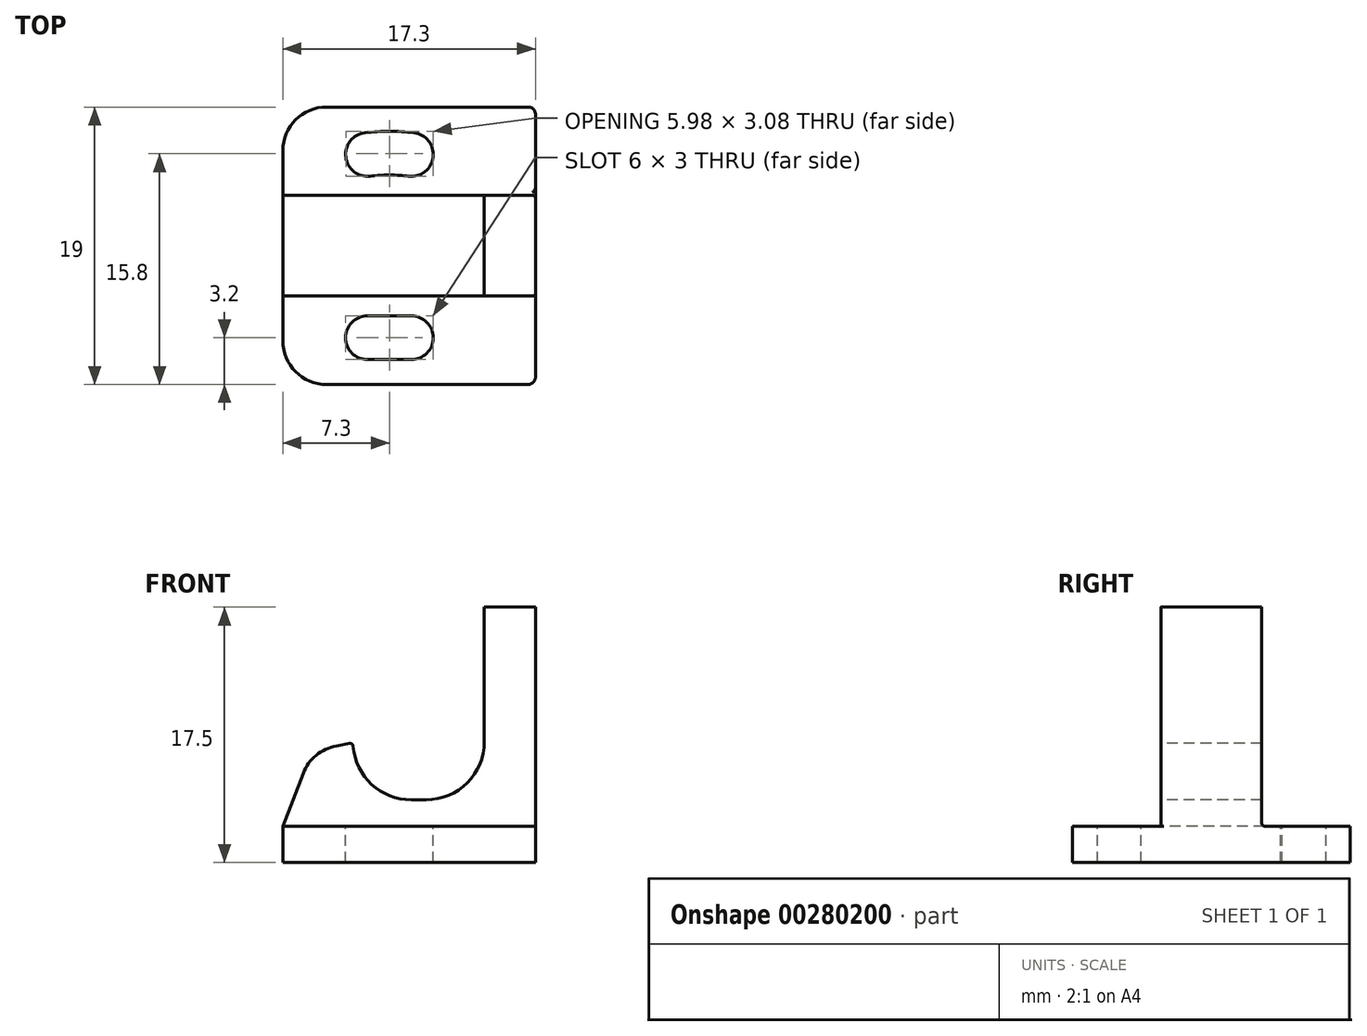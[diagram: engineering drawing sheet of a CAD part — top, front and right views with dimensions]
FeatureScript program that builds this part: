
annotation { "Feature Type Name" : "Feature", "Feature Type Description" : "" }
export const myFeature = defineFeature(function(context is Context, id is Id, definition is map)
    precondition{}
    {
        {
            var Q0;
            Q0=qCreatedBy(makeId("Top.planeOp"),FACE);
            var sketch = newSketch(context, id + "F0", { "sketchPlane" : qUnion([Q0])});
            skLineSegment(sketch, "E0.bottom", {"start": v(-8.65, 9.5) * mm, "end": v(8.65, 9.5) * mm});
            skLineSegment(sketch, "E0.top", {"start": v(-8.65, -9.5) * mm, "end": v(8.65, -9.5) * mm});
            skLineSegment(sketch, "E0.left", {"start": v(-8.65, 9.5) * mm, "end": v(-8.65, -9.5) * mm});
            skLineSegment(sketch, "E0.right", {"start": v(8.65, 9.5) * mm, "end": v(8.65, -9.5) * mm});
            skPoint(sketch, "E0.middle", {"position": v(0, 0) * mm});
            skSolve(sketch);
        }
        {
            var Q0;
            Q0=makeQuery(id+"F0.imprint","IMPRINT",FACE,{"disambiguationData":[TD([[makeQuery(id+"F0.imprint","IMPRINT",EDGE,{"derivedFrom":sQuery(id+"F0.wireOp",EDGE,"E0.bottom")}),-1.0]])]});
            extrude(context, id + "F1", {"entities" : qUnion([Q0]), "depth" : 2.5 * mm});
        }
        {
            var Q0;
            Q0=makeQuery(id+"F1.opExtrude","CAP_FACE",FACE,{"disambiguationData":[OSD([sQuery(id+"F0.wireOp",EDGE,"E0.bottom"),sQuery(id+"F0.wireOp",EDGE,"E0.top"),sQuery(id+"F0.wireOp",EDGE,"E0.left"),sQuery(id+"F0.wireOp",EDGE,"E0.right")])],"isStart":false});
            var sketch = newSketch(context, id + "F2", { "sketchPlane" : qUnion([Q0])});
            skLineSegment(sketch, "E1.bottom", {"start": v(-8.65, 3.45) * mm, "end": v(8.65, 3.45) * mm});
            skLineSegment(sketch, "E1.top", {"start": v(-8.65, -3.45) * mm, "end": v(8.65, -3.45) * mm});
            skLineSegment(sketch, "E1.left", {"start": v(-8.65, 3.45) * mm, "end": v(-8.65, -3.45) * mm});
            skLineSegment(sketch, "E1.right", {"start": v(8.65, 3.45) * mm, "end": v(8.65, -3.45) * mm});
            skLineSegment(sketch, "E2", {"start": v(-8.65, 0) * mm, "end": v(8.65, 0) * mm, "construction": true});
            skLineSegment(sketch, "E3.bottom", {"start": v(8.65, 3.45) * mm, "end": v(5.15, 3.45) * mm});
            skLineSegment(sketch, "E3.top", {"start": v(8.65, 9.5) * mm, "end": v(5.15, 9.5) * mm});
            skLineSegment(sketch, "E3.left", {"start": v(8.65, 3.45) * mm, "end": v(8.65, 9.5) * mm});
            skLineSegment(sketch, "E3.right", {"start": v(5.15, 3.45) * mm, "end": v(5.15, 9.5) * mm});
            skLineSegment(sketch, "E4.bottom", {"start": v(8.65, -3.45) * mm, "end": v(5.15, -3.45) * mm});
            skLineSegment(sketch, "E4.top", {"start": v(8.65, -9.5) * mm, "end": v(5.15, -9.5) * mm});
            skLineSegment(sketch, "E4.left", {"start": v(8.65, -3.45) * mm, "end": v(8.65, -9.5) * mm});
            skLineSegment(sketch, "E4.right", {"start": v(5.15, -3.45) * mm, "end": v(5.15, -9.5) * mm});
            skSolve(sketch);
        }
        {
            var Q0;
            Q0=makeQuery(id+"F2.imprint","IMPRINT",FACE,{"disambiguationData":[TD([[makeQuery(id+"F2.imprint","IMPRINT",EDGE,{"derivedFrom":sQuery(id+"F2.wireOp",EDGE,"E1.bottom")}),-1.0]])]});
            var Q1;
            Q1=makeQuery(id+"F2.imprint","IMPRINT",FACE,{"disambiguationData":[TD([[makeQuery(id+"F2.imprint","IMPRINT",EDGE,{"derivedFrom":sQuery(id+"F2.wireOp",EDGE,"E3.bottom")}),-1.0]])]});
            var Q2;
            Q2=makeQuery(id+"F2.imprint","IMPRINT",FACE,{"disambiguationData":[TD([[makeQuery(id+"F2.imprint","IMPRINT",EDGE,{"derivedFrom":sQuery(id+"F2.wireOp",EDGE,"E4.bottom")}),1.0]])]});
            extrude(context, id + "F3", {"entities" : qUnion([Q0, Q1, Q2]), "operationType" : NewBodyOperationType.ADD, "depth" : 15 * mm});
        }
        {
            var Q0;
            {var subQ0=sQuery(id+"F0.wireOp",EDGE,"E0.left");var subQ1=sQuery(id+"F0.wireOp",EDGE,"E0.top");Q0=makeQuery(id+"F3.boolean.opBoolean","SPLIT",FACE,{"disambiguationData":[TD([makeQuery(id+"F1.opExtrude","SWEPT_FACE",FACE,{"disambiguationData":[OSD([subQ1])]})])],"derivedFrom":makeQuery(id+"F1.opExtrude","CAP_FACE",FACE,{"disambiguationData":[OSD([sQuery(id+"F0.wireOp",EDGE,"E0.bottom"),subQ1,subQ0,sQuery(id+"F0.wireOp",EDGE,"E0.right")])],"isStart":false})});}
            var sketch = newSketch(context, id + "F4", { "sketchPlane" : qUnion([Q0])});
            skArc(sketch, "E5", {"start": v(-2.85, -4.8) * mm, "mid": v(-4.35, -6.3) * mm, "end": v(-2.85, -7.8) * mm});
            skArc(sketch, "E6", {"start": v(0.15, -7.8) * mm, "mid": v(1.65, -6.3) * mm, "end": v(0.15, -4.8) * mm});
            skLineSegment(sketch, "E7", {"start": v(-2.85, -4.8) * mm, "end": v(0.15, -4.8) * mm});
            skLineSegment(sketch, "E8", {"start": v(-2.85, -7.8) * mm, "end": v(0.15, -7.8) * mm});
            skPoint(sketch, "E9", {"position": v(-1.35, -6.3) * mm});
            skLineSegment(sketch, "E10", {"start": v(-1.35, -4.8) * mm, "end": v(-1.35, -7.8) * mm, "construction": true});
            skArc(sketch, "E11", {"start": v(1.63, 5.98) * mm, "mid": v(-1.35, 6.34) * mm, "end": v(-4.33, 5.98) * mm, "construction": true});
            skArc(sketch, "E12", {"start": v(-3.03, 7.74) * mm, "mid": v(-4.34, 6.07) * mm, "end": v(-2.67, 4.76) * mm});
            skArc(sketch, "E13", {"start": v(-0.03, 4.76) * mm, "mid": v(1.64, 6.07) * mm, "end": v(0.33, 7.74) * mm});
            skArc(sketch, "E14", {"start": v(0.33, 7.74) * mm, "mid": v(-1.35, 7.84) * mm, "end": v(-3.03, 7.74) * mm});
            skArc(sketch, "E15", {"start": v(-0.03, 4.76) * mm, "mid": v(-1.35, 4.84) * mm, "end": v(-2.67, 4.76) * mm});
            skLineSegment(sketch, "E16", {"start": v(-2.85, 6.25) * mm, "end": v(0.15, 6.25) * mm});
            skLineSegment(sketch, "E17", {"start": v(-1.35, 6.25) * mm, "end": v(-1.35, -6.3) * mm});
            skSolve(sketch);
        }
        {
            var Q0;
            {var subQ3=sQuery(id+"F4.wireOp",EDGE,"E12");Q0=makeQuery(id+"F4.imprint","IMPRINT",FACE,{"disambiguationData":[TD([[makeQuery(id+"F4.imprint","IMPRINT",EDGE,{"derivedFrom":subQ3}),1.0]])]});}
            var Q1;
            {var subQ3=sQuery(id+"F4.wireOp",EDGE,"E5");Q1=makeQuery(id+"F4.imprint","IMPRINT",FACE,{"disambiguationData":[TD([[makeQuery(id+"F4.imprint","IMPRINT",EDGE,{"derivedFrom":subQ3}),1.0]])]});}
            extrude(context, id + "F5", {"entities" : qUnion([Q0, Q1]), "operationType" : NewBodyOperationType.REMOVE, "oppositeDirection" : true, "depth" : 25 * mm});
        }
        {
            var Q0;
            Q0=qCreatedBy(makeId("Front.planeOp"),FACE);
            var sketch = newSketch(context, id + "F6", { "sketchPlane" : qUnion([Q0])});
            skLineSegment(sketch, "E18", {"start": v(-8.65, 2.5) * mm, "end": v(-6.65, 7.7) * mm});
            skArc(sketch, "E19", {"start": v(-3.85, 8.2) * mm, "mid": v(-2.64, 5.44) * mm, "end": v(0.15, 4.3) * mm});
            skLineSegment(sketch, "E20", {"start": v(0.15, 4.3) * mm, "end": v(1.15, 4.3) * mm});
            skLineSegment(sketch, "E21", {"start": v(-6.65, 7.7) * mm, "end": v(-3.85, 8.2) * mm});
            skArc(sketch, "E22", {"start": v(1.15, 4.3) * mm, "mid": v(3.98, 5.47) * mm, "end": v(5.15, 8.3) * mm});
            skLineSegment(sketch, "E23", {"start": v(5.15, 8.3) * mm, "end": v(5.15, 17.5) * mm});
            skLineSegment(sketch, "E24", {"start": v(5.15, 17.5) * mm, "end": v(-8.65, 17.5) * mm});
            skLineSegment(sketch, "E25", {"start": v(-8.65, 17.5) * mm, "end": v(-8.65, 2.5) * mm});
            skSolve(sketch);
        }
        {
            var Q0;
            Q0 = qSketchRegion(id + "F6", true);
            extrude(context, id + "F7", {"entities" : qUnion([Q0]), "operationType" : NewBodyOperationType.REMOVE, "endBound" : BoundingType.THROUGH_ALL, "oppositeDirection" : true, "depth" : 25 * mm, "hasSecondDirection" : true, "secondDirectionBound" : SecondDirectionBoundingType.THROUGH_ALL, "secondDirectionOppositeDirection" : false, "secondDirectionDepth" : 25 * mm});
        }
        {
            var Q0;
            Q0=makeQuery(id+"F3.boolean.opBoolean","MERGE",FACE,{"derivedFrom":[makeQuery(id+"F1.opExtrude","SWEPT_FACE",FACE,{"disambiguationData":[OSD([sQuery(id+"F0.wireOp",EDGE,"E0.right")])]}),makeQuery(id+"F3.opExtrude","SWEPT_FACE",FACE,{"disambiguationData":[OSD([sQuery(id+"F2.wireOp",EDGE,"E1.right"),sQuery(id+"F2.wireOp",EDGE,"E3.left"),sQuery(id+"F2.wireOp",EDGE,"E4.left")])]})]});
            var sketch = newSketch(context, id + "F8", { "sketchPlane" : qUnion([Q0])});
            skLineSegment(sketch, "E26", {"start": v(-9.5, 2.5) * mm, "end": v(-3.45, 17.5) * mm});
            skLineSegment(sketch, "E27", {"start": v(3.45, 17.5) * mm, "end": v(9.5, 2.5) * mm});
            skLineSegment(sketch, "E28", {"start": v(-3.45, 17.5) * mm, "end": v(-9.5, 17.5) * mm});
            skLineSegment(sketch, "E29", {"start": v(-9.5, 17.5) * mm, "end": v(-9.5, 2.5) * mm});
            skLineSegment(sketch, "E30", {"start": v(3.45, 17.5) * mm, "end": v(9.5, 17.5) * mm});
            skLineSegment(sketch, "E31", {"start": v(9.5, 17.5) * mm, "end": v(9.5, 2.5) * mm});
            skLineSegment(sketch, "E32", {"start": v(-3.5, 17.4) * mm, "end": v(3.5, 17.4) * mm});
            skLineSegment(sketch, "E33", {"start": v(-3.45, 17.5) * mm, "end": v(3.45, 17.5) * mm});
            skSolve(sketch);
        }
        {
            var Q0;
            Q0=makeQuery(id+"F8.imprint","IMPRINT",FACE,{"disambiguationData":[TD([[makeQuery(id+"F8.imprint","IMPRINT",EDGE,{"derivedFrom":sQuery(id+"F8.wireOp",EDGE,"E26")}),1.0]])]});
            var Q1;
            Q1=makeQuery(id+"F8.imprint","IMPRINT",FACE,{"disambiguationData":[TD([[makeQuery(id+"F8.imprint","IMPRINT",EDGE,{"derivedFrom":sQuery(id+"F8.wireOp",EDGE,"E27")}),1.0]])]});
            var Q2;
            {var subQ2=sQuery(id+"F8.wireOp",EDGE,"E32");Q2=makeQuery(id+"F8.imprint","IMPRINT",FACE,{"disambiguationData":[TD([[makeQuery(id+"F8.imprint","IMPRINT",EDGE,{"derivedFrom":subQ2}),1.0]])]});}
            extrude(context, id + "F9", {"entities" : qUnion([Q0, Q1, Q2]), "operationType" : NewBodyOperationType.REMOVE, "oppositeDirection" : true, "depth" : 25 * mm});
        }
        {
            var Q0;
            Q0=makeQuery(id+"F7.boolean.opBoolean","COPY",EDGE,{"derivedFrom":makeQuery(id+"F7.opExtrude","SWEPT_EDGE",EDGE,{"disambiguationData":[OSD([sQuery(id+"F6.wireOp",EDGE,"E18"),sQuery(id+"F6.wireOp",EDGE,"E21")])]})});
            fillet(context, id + "F10", {"entities" : qUnion([Q0]), "radius" : 3 * mm, "tangentPropagation" : true, "allowEdgeOverflow" : false});
        }
        {
            var Q0;
            Q0=makeQuery(id+"F1.opExtrude","SWEPT_EDGE",EDGE,{"disambiguationData":[OSD([sQuery(id+"F0.wireOp",EDGE,"E0.bottom"),sQuery(id+"F0.wireOp",EDGE,"E0.left")])]});
            var Q1;
            Q1=makeQuery(id+"F1.opExtrude","SWEPT_EDGE",EDGE,{"disambiguationData":[OSD([sQuery(id+"F0.wireOp",EDGE,"E0.top"),sQuery(id+"F0.wireOp",EDGE,"E0.left")])]});
            fillet(context, id + "F11", {"entities" : qUnion([Q0, Q1]), "radius" : 3 * mm, "tangentPropagation" : true, "allowEdgeOverflow" : false});
        }
        {
            var Q0;
            Q0=makeQuery(id+"F7.boolean.opBoolean","COPY",EDGE,{"derivedFrom":makeQuery(id+"F7.opExtrude","SWEPT_EDGE",EDGE,{"disambiguationData":[OSD([sQuery(id+"F6.wireOp",EDGE,"E19"),sQuery(id+"F6.wireOp",EDGE,"E21")])]})});
            var Q1;
            Q1=makeQuery(id+"F9.boolean.opBoolean","INTERSECT",EDGE,{"derivedFrom":[makeQuery(id+"F7.boolean.opBoolean","MERGE",FACE,{"derivedFrom":[makeQuery(id+"F3.opExtrude","SWEPT_FACE",FACE,{"disambiguationData":[OSD([sQuery(id+"F2.wireOp",EDGE,"E3.right")])]}),makeQuery(id+"F3.opExtrude","SWEPT_FACE",FACE,{"disambiguationData":[OSD([sQuery(id+"F2.wireOp",EDGE,"E4.right")])]}),makeQuery(id+"F7.opExtrude","SWEPT_FACE",FACE,{"disambiguationData":[OSD([sQuery(id+"F6.wireOp",EDGE,"E23")])]})]}),makeQuery(id+"F9.opExtrude","SWEPT_FACE",FACE,{"disambiguationData":[OSD([sQuery(id+"F8.wireOp",EDGE,"E32")])]})]});
            var Q2;
            Q2=makeQuery(id+"F3.opExtrude","CAP_EDGE",EDGE,{"disambiguationData":[OSD([sQuery(id+"F2.wireOp",EDGE,"E1.bottom")])],"isStart":true});
            var Q3;
            Q3=makeQuery(id+"F3.opExtrude","CAP_EDGE",EDGE,{"disambiguationData":[OSD([sQuery(id+"F2.wireOp",EDGE,"E1.top")])],"isStart":true});
            var Q4;
            Q4=makeQuery(id+"F3.opExtrude","CAP_EDGE",EDGE,{"disambiguationData":[OSD([sQuery(id+"F2.wireOp",EDGE,"E4.right")])],"isStart":true});
            var Q5;
            Q5=makeQuery(id+"F3.opExtrude","CAP_EDGE",EDGE,{"disambiguationData":[OSD([sQuery(id+"F2.wireOp",EDGE,"E3.right")])],"isStart":true});
            var Q6;
            Q6=makeQuery(id+"F3.opExtrude","SWEPT_EDGE",EDGE,{"disambiguationData":[OSD([sQuery(id+"F2.wireOp",EDGE,"E1.top"),sQuery(id+"F2.wireOp",EDGE,"E4.bottom"),sQuery(id+"F2.wireOp",EDGE,"E4.right")])]});
            var Q7;
            Q7=makeQuery(id+"F3.opExtrude","SWEPT_EDGE",EDGE,{"disambiguationData":[OSD([sQuery(id+"F2.wireOp",EDGE,"E1.bottom"),sQuery(id+"F2.wireOp",EDGE,"E3.bottom"),sQuery(id+"F2.wireOp",EDGE,"E3.right")])]});
            fillet(context, id + "F12", {"entities" : qUnion([Q0, Q1, Q2, Q3, Q4, Q5, Q6, Q7]), "radius" : 0.2 * mm, "tangentPropagation" : true, "allowEdgeOverflow" : false});
        }
        {
            var Q0;
            Q0=makeQuery(id+"F9.boolean.opBoolean","INTERSECT",EDGE,{"derivedFrom":[makeQuery(id+"F7.boolean.opBoolean","MERGE",FACE,{"derivedFrom":[makeQuery(id+"F3.opExtrude","SWEPT_FACE",FACE,{"disambiguationData":[OSD([sQuery(id+"F2.wireOp",EDGE,"E3.right")])]}),makeQuery(id+"F3.opExtrude","SWEPT_FACE",FACE,{"disambiguationData":[OSD([sQuery(id+"F2.wireOp",EDGE,"E4.right")])]}),makeQuery(id+"F7.opExtrude","SWEPT_FACE",FACE,{"disambiguationData":[OSD([sQuery(id+"F6.wireOp",EDGE,"E23")])]})]}),makeQuery(id+"F9.opExtrude","SWEPT_FACE",FACE,{"disambiguationData":[OSD([sQuery(id+"F8.wireOp",EDGE,"E26")])]})]});
            var Q1;
            Q1=makeQuery(id+"F9.boolean.opBoolean","COPY",EDGE,{"derivedFrom":makeQuery(id+"F9.opExtrude","CAP_EDGE",EDGE,{"disambiguationData":[OSD([sQuery(id+"F8.wireOp",EDGE,"E26")])],"isStart":true})});
            var Q2;
            Q2=makeQuery(id+"F9.boolean.opBoolean","COPY",EDGE,{"derivedFrom":makeQuery(id+"F9.opExtrude","SWEPT_EDGE",EDGE,{"disambiguationData":[OSD([sQuery(id+"F8.wireOp",EDGE,"E26"),sQuery(id+"F8.wireOp",EDGE,"E32")])]})});
            var Q3;
            Q3=makeQuery(id+"F9.boolean.opBoolean","COPY",EDGE,{"derivedFrom":makeQuery(id+"F9.opExtrude","CAP_EDGE",EDGE,{"disambiguationData":[OSD([sQuery(id+"F8.wireOp",EDGE,"E27")])],"isStart":true})});
            var Q4;
            Q4=makeQuery(id+"F9.boolean.opBoolean","INTERSECT",EDGE,{"derivedFrom":[makeQuery(id+"F7.boolean.opBoolean","MERGE",FACE,{"derivedFrom":[makeQuery(id+"F3.opExtrude","SWEPT_FACE",FACE,{"disambiguationData":[OSD([sQuery(id+"F2.wireOp",EDGE,"E3.right")])]}),makeQuery(id+"F3.opExtrude","SWEPT_FACE",FACE,{"disambiguationData":[OSD([sQuery(id+"F2.wireOp",EDGE,"E4.right")])]}),makeQuery(id+"F7.opExtrude","SWEPT_FACE",FACE,{"disambiguationData":[OSD([sQuery(id+"F6.wireOp",EDGE,"E23")])]})]}),makeQuery(id+"F9.opExtrude","SWEPT_FACE",FACE,{"disambiguationData":[OSD([sQuery(id+"F8.wireOp",EDGE,"E27")])]})]});
            var Q5;
            Q5=makeQuery(id+"F9.boolean.opBoolean","COPY",EDGE,{"derivedFrom":makeQuery(id+"F9.opExtrude","SWEPT_EDGE",EDGE,{"disambiguationData":[OSD([sQuery(id+"F8.wireOp",EDGE,"E27"),sQuery(id+"F8.wireOp",EDGE,"E32")])]})});
            var Q6;
            Q6=makeQuery(id+"F3.boolean.opBoolean","MERGE",EDGE,{"derivedFrom":[makeQuery(id+"F1.opExtrude","SWEPT_EDGE",EDGE,{"disambiguationData":[OSD([sQuery(id+"F0.wireOp",EDGE,"E0.bottom"),sQuery(id+"F0.wireOp",EDGE,"E0.right")])]}),makeQuery(id+"F3.opExtrude","SWEPT_EDGE",EDGE,{"disambiguationData":[OSD([sQuery(id+"F2.wireOp",EDGE,"E3.top"),sQuery(id+"F2.wireOp",EDGE,"E3.left")])]})]});
            var Q7;
            Q7=makeQuery(id+"F3.boolean.opBoolean","MERGE",EDGE,{"derivedFrom":[makeQuery(id+"F1.opExtrude","SWEPT_EDGE",EDGE,{"disambiguationData":[OSD([sQuery(id+"F0.wireOp",EDGE,"E0.top"),sQuery(id+"F0.wireOp",EDGE,"E0.right")])]}),makeQuery(id+"F3.opExtrude","SWEPT_EDGE",EDGE,{"disambiguationData":[OSD([sQuery(id+"F2.wireOp",EDGE,"E4.top"),sQuery(id+"F2.wireOp",EDGE,"E4.left")])]})]});
            var Q8;
            Q8=makeQuery(id+"F9.boolean.opBoolean","COPY",EDGE,{"derivedFrom":makeQuery(id+"F9.opExtrude","CAP_EDGE",EDGE,{"disambiguationData":[OSD([sQuery(id+"F8.wireOp",EDGE,"E32")])],"isStart":true})});
            fillet(context, id + "F13", {"entities" : qUnion([Q0, Q1, Q2, Q3, Q4, Q5, Q6, Q7, Q8]), "radius" : 0.5 * mm, "tangentPropagation" : true, "allowEdgeOverflow" : false});
        }
    });
